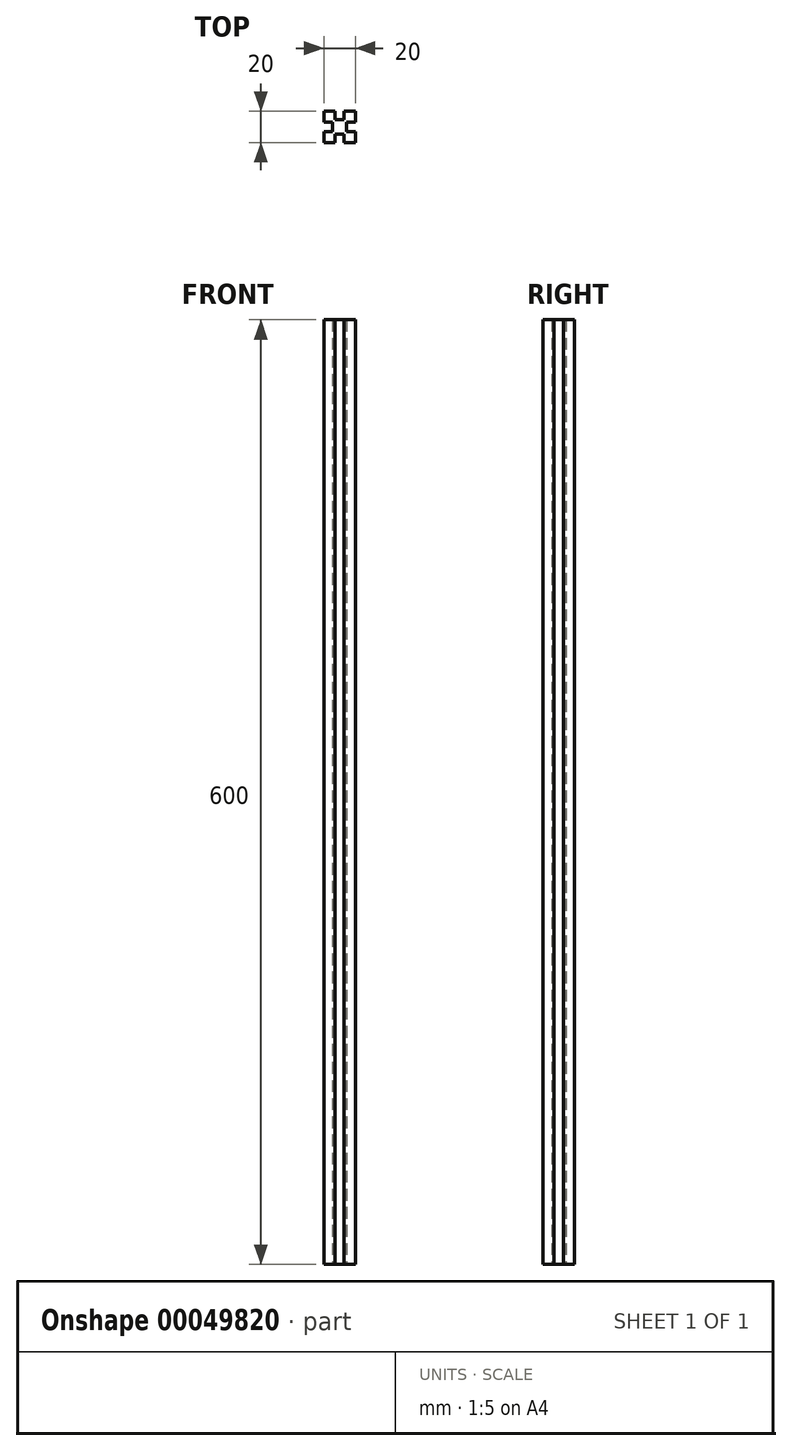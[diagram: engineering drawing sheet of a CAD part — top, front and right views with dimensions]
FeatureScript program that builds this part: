
annotation { "Feature Type Name" : "Feature", "Feature Type Description" : "" }
export const myFeature = defineFeature(function(context is Context, id is Id, definition is map)
    precondition{}
    {
        {
            var Q0;
            Q0=qCreatedBy(makeId("Top.planeOp"),FACE);
            var sketch = newSketch(context, id + "F0", { "sketchPlane" : qUnion([Q0])});
            skLineSegment(sketch, "E0.bottom", {"start": v(0, 0) * mm, "end": v(20, 0) * mm});
            skLineSegment(sketch, "E0.top", {"start": v(0, 20) * mm, "end": v(20, 20) * mm});
            skLineSegment(sketch, "E0.left", {"start": v(0, 0) * mm, "end": v(0, 20) * mm});
            skLineSegment(sketch, "E0.right", {"start": v(20, 0) * mm, "end": v(20, 20) * mm});
            skLineSegment(sketch, "E1.bottom", {"start": v(7, 20) * mm, "end": v(13, 20) * mm});
            skLineSegment(sketch, "E1.top", {"start": v(7, 14.5) * mm, "end": v(13, 14.5) * mm});
            skLineSegment(sketch, "E1.left", {"start": v(7, 20) * mm, "end": v(7, 14.5) * mm});
            skLineSegment(sketch, "E1.right", {"start": v(13, 20) * mm, "end": v(13, 14.5) * mm});
            skLineSegment(sketch, "E2.bottom", {"start": v(20, 13) * mm, "end": v(14.5, 13) * mm});
            skLineSegment(sketch, "E2.top", {"start": v(20, 7) * mm, "end": v(14.5, 7) * mm});
            skLineSegment(sketch, "E2.left", {"start": v(20, 13) * mm, "end": v(20, 7) * mm});
            skLineSegment(sketch, "E2.right", {"start": v(14.5, 13) * mm, "end": v(14.5, 7) * mm});
            skLineSegment(sketch, "E3.bottom", {"start": v(13, 0) * mm, "end": v(7, 0) * mm});
            skLineSegment(sketch, "E3.top", {"start": v(13, 5.5) * mm, "end": v(7, 5.5) * mm});
            skLineSegment(sketch, "E3.left", {"start": v(13, 0) * mm, "end": v(13, 5.5) * mm});
            skLineSegment(sketch, "E3.right", {"start": v(7, 0) * mm, "end": v(7, 5.5) * mm});
            skLineSegment(sketch, "E4.bottom", {"start": v(0, 7) * mm, "end": v(5.5, 7) * mm});
            skLineSegment(sketch, "E4.top", {"start": v(0, 13) * mm, "end": v(5.5, 13) * mm});
            skLineSegment(sketch, "E4.left", {"start": v(0, 7) * mm, "end": v(0, 13) * mm});
            skLineSegment(sketch, "E4.right", {"start": v(5.5, 7) * mm, "end": v(5.5, 13) * mm});
            skSolve(sketch);
        }
        {
            var Q0;
            Q0=makeQuery(id+"F0.imprint","IMPRINT",FACE,{"disambiguationData":[TD([[makeQuery(id+"F0.imprint","IMPRINT",EDGE,{"derivedFrom":sQuery(id+"F0.wireOp",EDGE,"E1.top")}),-1.0]])]});
            extrude(context, id + "F1", {"entities" : qUnion([Q0]), "depth" : 600 * mm});
        }
    });
